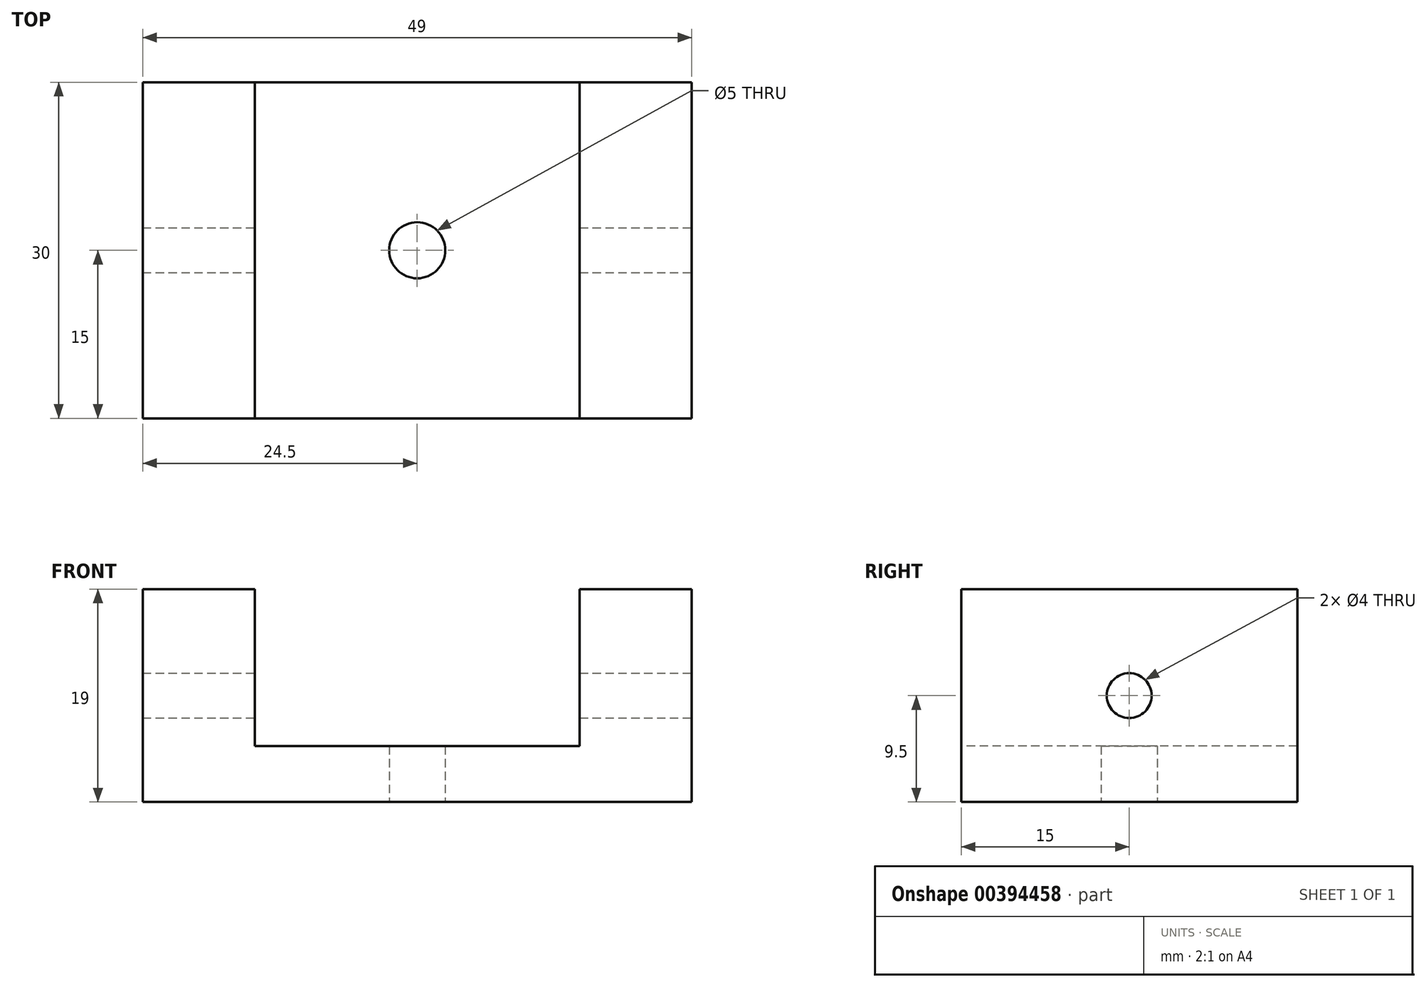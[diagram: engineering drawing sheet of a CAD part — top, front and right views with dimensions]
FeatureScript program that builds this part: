
annotation { "Feature Type Name" : "Feature", "Feature Type Description" : "" }
export const myFeature = defineFeature(function(context is Context, id is Id, definition is map)
    precondition{}
    {
        {
            var Q0;
            Q0=qCreatedBy(makeId("Top.planeOp"),FACE);
            var sketch = newSketch(context, id + "F0", { "sketchPlane" : qUnion([Q0])});
            skLineSegment(sketch, "E0.bottom", {"start": v(24.5, 15) * mm, "end": v(-24.5, 15) * mm});
            skLineSegment(sketch, "E0.top", {"start": v(24.5, -15) * mm, "end": v(-24.5, -15) * mm});
            skLineSegment(sketch, "E0.left", {"start": v(24.5, 15) * mm, "end": v(24.5, -15) * mm});
            skLineSegment(sketch, "E0.right", {"start": v(-24.5, 15) * mm, "end": v(-24.5, -15) * mm});
            skPoint(sketch, "E0.middle", {"position": v(0, 0) * mm});
            skLineSegment(sketch, "E1", {"start": v(-14.5, 15) * mm, "end": v(-14.5, -15) * mm});
            skLineSegment(sketch, "E2", {"start": v(14.5, 15) * mm, "end": v(14.5, -15) * mm});
            skCircle(sketch, "E3", {"center": v(0, 0) * mm, "radius": 2.5 * mm});
            skSolve(sketch);
        }
        {
            var Q0;
            {var subQ0=sQuery(id+"F0.wireOp",EDGE,"E1");Q0=makeQuery(id+"F0.imprint","IMPRINT",FACE,{"disambiguationData":[TD([[makeQuery(id+"F0.imprint","IMPRINT",EDGE,{"derivedFrom":subQ0}),1.0]])]});}
            extrude(context, id + "F1", {"entities" : qUnion([Q0]), "depth" : 5 * mm});
        }
        {
            var Q0;
            {var subQ0=sQuery(id+"F0.wireOp",EDGE,"E0.right");Q0=makeQuery(id+"F0.imprint","IMPRINT",FACE,{"disambiguationData":[TD([[makeQuery(id+"F0.imprint","IMPRINT",EDGE,{"derivedFrom":subQ0}),1.0]])]});}
            extrude(context, id + "F2", {"entities" : qUnion([Q0]), "operationType" : NewBodyOperationType.ADD, "depth" : 19 * mm});
        }
        {
            var Q0;
            {var subQ0=sQuery(id+"F0.wireOp",EDGE,"E0.left");Q0=makeQuery(id+"F0.imprint","IMPRINT",FACE,{"disambiguationData":[TD([[makeQuery(id+"F0.imprint","IMPRINT",EDGE,{"derivedFrom":subQ0}),-1.0]])]});}
            extrude(context, id + "F3", {"entities" : qUnion([Q0]), "operationType" : NewBodyOperationType.ADD, "depth" : 19 * mm});
        }
        {
            var Q0;
            Q0=makeQuery(id+"F3.opExtrude","SWEPT_FACE",FACE,{"disambiguationData":[OSD([sQuery(id+"F0.wireOp",EDGE,"E0.left")])]});
            var sketch = newSketch(context, id + "F4", { "sketchPlane" : qUnion([Q0])});
            skCircle(sketch, "E4", {"center": v(0, 9.5) * mm, "radius": 2 * mm});
            skPoint(sketch, "E4.centerSnap0", {"position": v(-15, 9.5) * mm});
            skSolve(sketch);
        }
        {
            var Q0;
            Q0=makeQuery(id+"F4.imprint","IMPRINT",FACE,{"disambiguationData":[TD([[makeQuery(id+"F4.imprint","IMPRINT",EDGE,{"derivedFrom":sQuery(id+"F4.wireOp",EDGE,"E4")}),1.0]])]});
            extrude(context, id + "F5", {"entities" : qUnion([Q0]), "operationType" : NewBodyOperationType.REMOVE, "endBound" : BoundingType.THROUGH_ALL, "oppositeDirection" : true, "depth" : 25 * mm});
        }
    });
